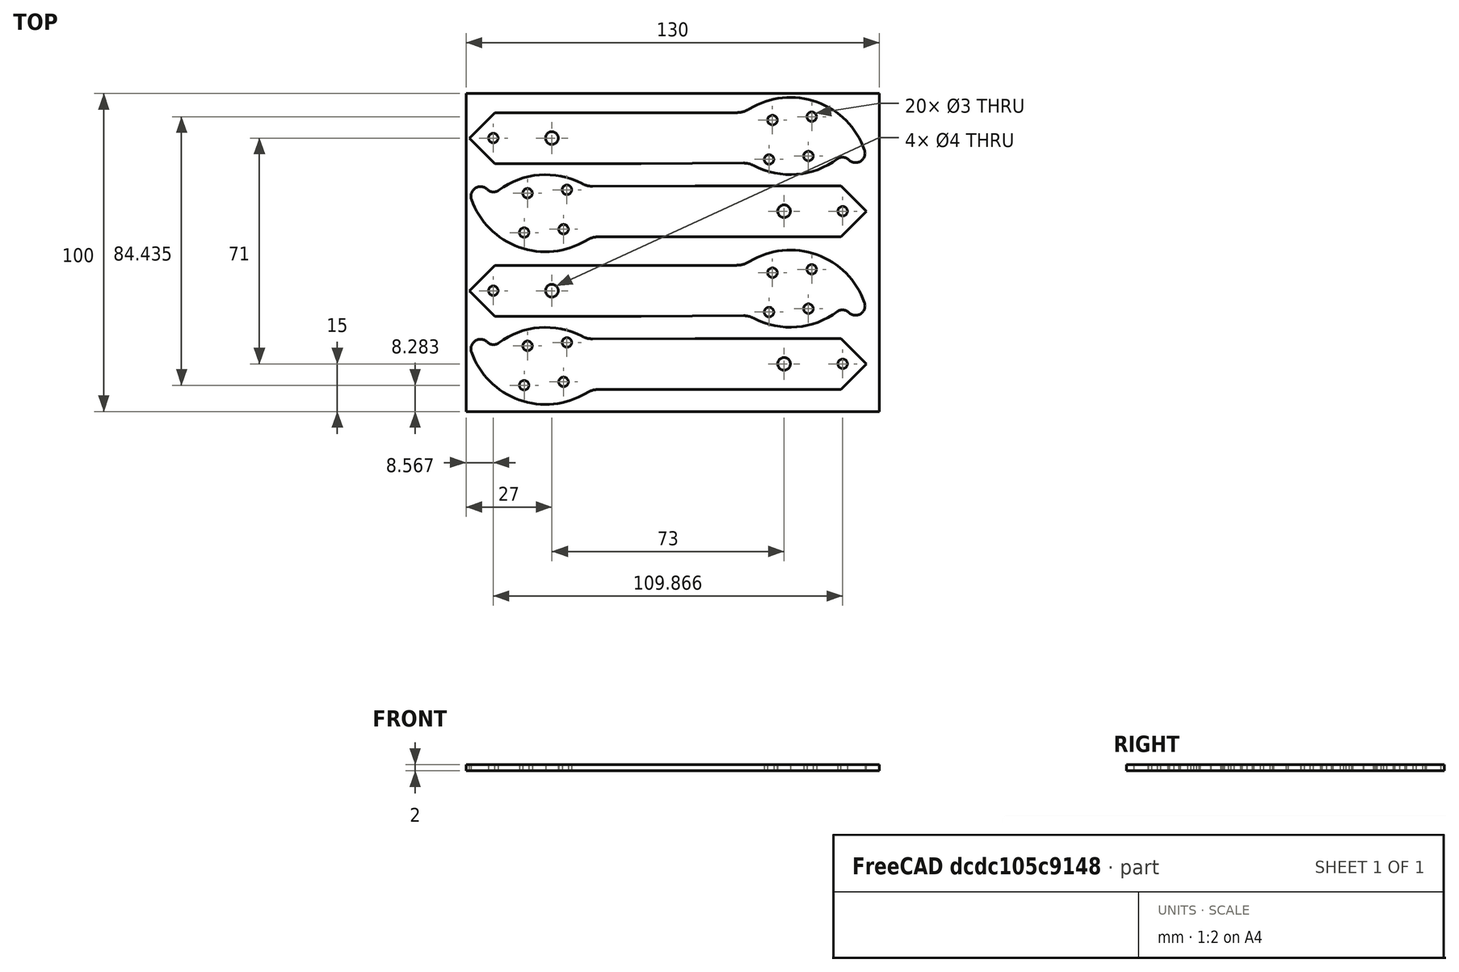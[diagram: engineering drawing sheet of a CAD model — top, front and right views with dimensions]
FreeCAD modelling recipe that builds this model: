
FCSTD DOCUMENT  (FreeCAD 0.18RUnknown)
Label: cam_arm_left
License: All rights reserved
LicenseURL: http://en.wikipedia.org/wiki/All_rights_reserved
objects: Path::FeaturePython×6, Part::FeaturePython×6, App::FeaturePython×1, Part::MultiFuse×1, App::DocumentObjectGroup×1, Path::FeatureCompoundPython×1
note: 8 computed .brp shape members not serialized (recipe doc carries the construction recipe); baked Part::Feature solids carry a one-line shape summary decoded from their .brp

FEATURE [App::FeaturePython] SetupSheet  # Path/CAM operation (typed FeaturePython)
  ClearanceHeightExpression = StartDepth+SetupSheet.ClearanceHeightOffset
  ClearanceHeightOffset = 4
  FinalDepthExpression = OpFinalDepth
  HorizRapid = 0
  SafeHeightExpression = StartDepth+SetupSheet.SafeHeightOffset
  SafeHeightOffset = 4
  StartDepthExpression = OpStartDepth
  StepDownExpression = OpToolDiameter
  VertRapid = 0
FEATURE [Path::FeaturePython] Default_Tool  label="Default Tool"  # Path/CAM operation (typed FeaturePython)
  HorizFeed = 10
  HorizRapid = 0
  SpindleDir = 0
  SpindleSpeed = 24000
  ToolNumber = 1
  VertFeed = 1.66667
  VertRapid = 0
  expr: Tool.Diameter = 3.175
  expr: VertFeed = 100mm / min
  expr: HorizFeed = 600mm / min
  expr: HorizRapid = SetupSheet.HorizRapid
  expr: VertRapid = SetupSheet.VertRapid
FEATURE [Path::FeaturePython] Contour  # Path/CAM operation (typed FeaturePython)
  Active = true
  AreaParams:
    OpenMode = 0
    Angle = 45.0
    MinArcPoints = 4
    Coplanar = 2
    Tolerance = 1e-07
    CleanDistance = 0.0
    PocketExtraOffset = 0.0
    RoundPrecision = 0.0
    AngleShift = 0.0
    SubjectFill = 0
    PocketMode = 0
    Simplify = False
    SectionTolerance = 1e-06
    MaxArcPoints = 100
    Offset = 1.5875
    Accuracy = 0.01
    PocketStepover = 0.0
    ClipFill = 0
    ToolRadius = 1.0
    Outline = False
    ClipperScale = 10000000.0
    FromCenter = False
    Explode = False
    EndType = 0
    Shift = 0.0
    ExtraPass = 0
    Project = False
    JoinType = 0
    Thicken = False
    Stepdown = 1.0
    SectionMode = 2
    MiterLimit = 2.0
    Deflection = 0.01
    Reorient = True
    FitArcs = True
    SectionCount = -1
    SectionOffset = 0.0
    Stepover = 0.0
    Unit = 1.0
    Fill = 0
  ClearanceHeight = 4
  Direction = 0
  FinalDepth = -3
  JoinType = 0
  MiterLimit = 0.1
  OffsetExtra = 0
  OpFinalDepth = -2
  OpStartDepth = 0
  OpStockZMax = 0
  OpStockZMin = 0
  OpToolDiameter = 3.175
  PathParams = {'resume_height': 4.0, 'feedrate': 10.0, 'verbose': True, 'orientation': 1, 'return_end': True, 'preamble': False, 'retraction': 4.0, 'feedrate_v': 1.6666666666666667}
  SafeHeight = 4
  Side = 0
  StartDepth = 0
  StartPoint = (0,0,0)
  StepDown = 0.5
  ToolController = -> Default_Tool
  UseComp = true
  UseStartPoint = false
  expr: ClearanceHeight = StartDepth + SetupSheet.ClearanceHeightOffset
  expr: SafeHeight = StartDepth + SetupSheet.SafeHeightOffset
  expr: StepDown = 0.5
  expr: StartDepth = OpStartDepth
FEATURE [Path::FeaturePython] T2__drill  label="T2: drill"  # Path/CAM operation (typed FeaturePython)
  HorizFeed = 10
  HorizRapid = 0
  SpindleDir = 0
  SpindleSpeed = 10000
  ToolNumber = 2
  VertFeed = 1.66667
  VertRapid = 0
  expr: VertFeed = 100mm / min
  expr: HorizFeed = 600mm / min
  expr: HorizRapid = SetupSheet.HorizRapid
  expr: VertRapid = SetupSheet.VertRapid
FEATURE [Part::FeaturePython] Stock001  # WARN: FeaturePython — macro-defined, semantics opaque (R4)
  Height = 2
  Length = 130
  Placement = pos=(0,0,-2) rot=(0,0,1;0rad)
  StockType = CreateBox
  Width = 100
FEATURE [Part::FeaturePython] arm_left_01  # a2plus imported part (geometry in sourceFile) (typed FeaturePython)
  Placement = pos=(25,15,0) rot=(0,0,1;1.5708rad)
  fixedPosition = true
  sourceFile = <userpath>/hs/fly/cad/arm_left.fcstd
  timeLastImport = 1.55482e+09
  updateColors = true
FEATURE [Part::FeaturePython] arm_left_002  # a2plus imported part (geometry in sourceFile) (typed FeaturePython)
  Placement = pos=(102,38,0) rot=(0,0,-1;1.5708rad)
  fixedPosition = true
  sourceFile = <userpath>/hs/fly/cad/arm_left.fcstd
  timeLastImport = 1.55482e+09
  updateColors = true
FEATURE [Part::FeaturePython] arm_left_003  # a2plus imported part (geometry in sourceFile) (typed FeaturePython)
  Placement = pos=(25,63,0) rot=(0,0,1;1.5708rad)
  fixedPosition = true
  sourceFile = <userpath>/hs/fly/cad/arm_left.fcstd
  timeLastImport = 1.55482e+09
  updateColors = true
FEATURE [Part::FeaturePython] arm_left_004  # a2plus imported part (geometry in sourceFile) (typed FeaturePython)
  Placement = pos=(102,86,0) rot=(0,0,-1;1.5708rad)
  fixedPosition = true
  sourceFile = <userpath>/hs/fly/cad/arm_left.fcstd
  timeLastImport = 1.55482e+09
  updateColors = true
FEATURE [Part::MultiFuse] Fusion
  Shapes = -> [arm_left_01,arm_left_002,arm_left_003,arm_left_004]
FEATURE [Part::FeaturePython] Clone  label="Base-arm_01"  # Draft clone (typed FeaturePython)
  AttacherType = Attacher::AttachEngine3D
  Fuse = false
  Objects = -> [Fusion]
  PathResource = Base
  Scale = (1,1,1)
FEATURE [Path::FeaturePython] Drilling  # Path/CAM operation (typed FeaturePython)
  Active = true
  AddTipLength = false
  Base = -> [Clone]
  ClearanceHeight = 4
  DwellEnabled = false
  DwellTime = 0
  FinalDepth = -3
  OpFinalDepth = -2
  OpStartDepth = 0
  OpStockZMax = 0
  OpStockZMin = 0
  OpToolDiameter = 3
  PeckDepth = 0
  PeckEnabled = false
  RetractHeight = 10
  ReturnLevel = 0
  SafeHeight = 4
  StartDepth = 0
  ToolController = -> T2__drill
  expr: ClearanceHeight = StartDepth + SetupSheet.ClearanceHeightOffset
  expr: SafeHeight = StartDepth + SetupSheet.SafeHeightOffset
  expr: FinalDepth = -3
  expr: StartDepth = OpStartDepth
FEATURE [Path::FeaturePython] TagDressup  # Path/CAM operation (typed FeaturePython)
  Angle = 45
  Base = -> Contour
  Disabled = [12,13]
  Height = 4
  Positions = (16) [(100.27,5.41,0),(52.73,5.41,0),(51.89,24.5,0),(90.86,24.59,0),(77.32,28.51,0),(37.01,28.41,0),(35.5,47.59,0),(76.67,47.59,0),(86.44,53.41,0),+7 more]
  Radius = 0
  SegmentationFactor = 50
  Width = 7.59
FEATURE [App::DocumentObjectGroup] Model  label="Unnamed001"
  Group = -> [Clone]
FEATURE [Path::FeatureCompoundPython] Operations001  label="Operations"  # Path/CAM operation (typed FeaturePython)
  Group = -> [Drilling,TagDressup]
  UsePlacements = false
FEATURE [Path::FeaturePython] Job  # Path/CAM operation (typed FeaturePython)
  GeometryTolerance = 0.01
  Model = -> Model
  Operations = -> Operations001
  PostProcessor = 5
  PostProcessorOutputFile = <userpath>/hs/fly/cad/gcode/arm
  SetupSheet = -> SetupSheet
  Stock = -> Stock001
  ToolController = -> [Default_Tool,T2__drill]
